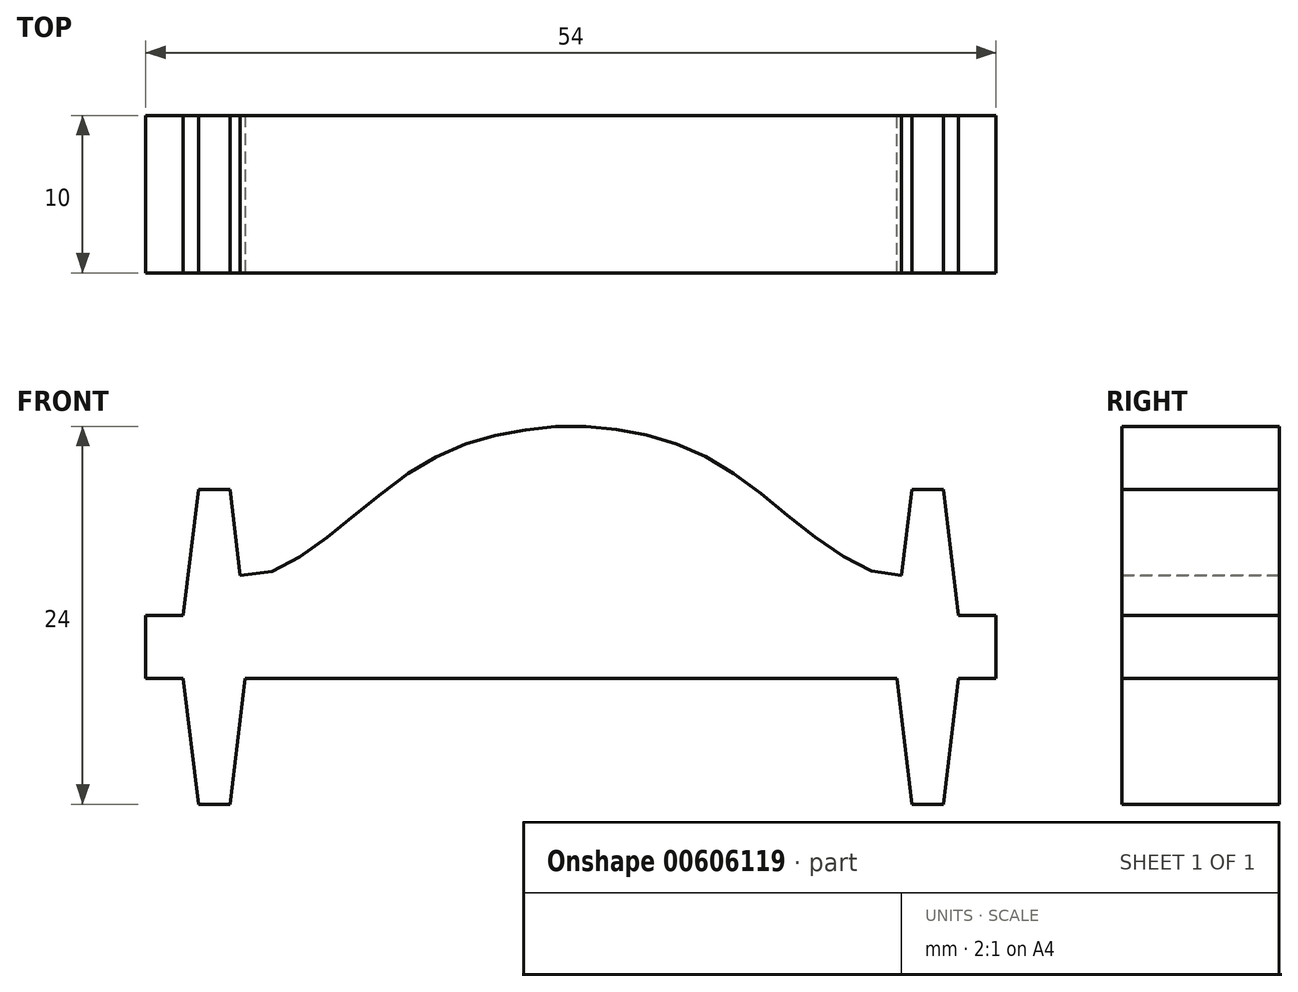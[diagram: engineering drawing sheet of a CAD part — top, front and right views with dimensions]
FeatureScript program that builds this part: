
annotation { "Feature Type Name" : "Feature", "Feature Type Description" : "" }
export const myFeature = defineFeature(function(context is Context, id is Id, definition is map)
    precondition{}
    {
        {
            var Q0;
            Q0=qCreatedBy(makeId("Front.planeOp"),FACE);
            var sketch = newSketch(context, id + "F0", { "sketchPlane" : qUnion([Q0])});
            skLineSegment(sketch, "E0", {"start": v(21, 26.44) * mm, "end": v(-21, 26.44) * mm});
            skFitSpline(sketch, "E1", {"points": [v(-21, 28.98) * mm, v(-17.48, 29.98) * mm, v(-13.98, 32.6) * mm, v(-10.48, 35.33) * mm, v(-6.98, 37.21) * mm, v(-3.48, 38.13) * mm, v(0, 38.44) * mm, v(3.5, 38.13) * mm, v(7, 37.21) * mm, v(10.5, 35.33) * mm, v(14, 32.6) * mm, v(17.63, 29.98) * mm, v(21, 28.98) * mm], "startDerivative": vector(52.28, -5.2) * mm, "endDerivative": vector(46.1, 5.3) * mm});
            skLineSegment(sketch, "E2", {"start": v(-21, 28.98) * mm, "end": v(-21, 26.44) * mm});
            skLineSegment(sketch, "E3", {"start": v(21, 28.98) * mm, "end": v(21, 26.44) * mm});
            skLineSegment(sketch, "E4", {"start": v(-3.48, 38.13) * mm, "end": v(3.5, 38.13) * mm, "construction": true});
            skLineSegment(sketch, "E5", {"start": v(7, 37.21) * mm, "end": v(-6.98, 37.21) * mm, "construction": true});
            skLineSegment(sketch, "E6", {"start": v(-10.48, 35.33) * mm, "end": v(10.5, 35.33) * mm, "construction": true});
            skLineSegment(sketch, "E7", {"start": v(14, 32.6) * mm, "end": v(-13.98, 32.6) * mm, "construction": true});
            skLineSegment(sketch, "E8", {"start": v(-17.48, 29.98) * mm, "end": v(17.63, 29.98) * mm, "construction": true});
            skSolve(sketch);
        }
        {
            var Q0;
            Q0=qCreatedBy(makeId("Front.planeOp"),FACE);
            var sketch = newSketch(context, id + "F1", { "sketchPlane" : qUnion([Q0])});
            skLineSegment(sketch, "E9", {"start": v(-27, 26.44) * mm, "end": v(27, 26.44) * mm});
            skLineSegment(sketch, "E10", {"start": v(27, 26.44) * mm, "end": v(27, 22.44) * mm});
            skLineSegment(sketch, "E11", {"start": v(27, 22.44) * mm, "end": v(-27, 22.44) * mm});
            skLineSegment(sketch, "E12", {"start": v(-27, 22.44) * mm, "end": v(-27, 26.44) * mm});
            skPoint(sketch, "E13", {"position": v(0, 22.44) * mm});
            skSolve(sketch);
        }
        {
            var Q0;
            Q0 = qSketchRegion(id + "F1", true);
            extrude(context, id + "F2", {"entities" : qUnion([Q0]), "endBound" : BoundingType.SYMMETRIC, "depth" : 10 * mm, "offsetDistance" : 25 * mm});
        }
        {
            var Q0;
            Q0=qCreatedBy(makeId("Front.planeOp"),FACE);
            var sketch = newSketch(context, id + "F3", { "sketchPlane" : qUnion([Q0])});
            skLineSegment(sketch, "E14", {"start": v(20.46, 24.44) * mm, "end": v(21.66, 34.44) * mm});
            skLineSegment(sketch, "E15", {"start": v(21.66, 34.44) * mm, "end": v(23.66, 34.44) * mm});
            skLineSegment(sketch, "E16", {"start": v(23.66, 14.44) * mm, "end": v(21.66, 14.44) * mm});
            skLineSegment(sketch, "E17", {"start": v(21.66, 14.44) * mm, "end": v(20.46, 24.44) * mm});
            skLineSegment(sketch, "E18", {"start": v(23.66, 34.44) * mm, "end": v(24.86, 24.44) * mm});
            skLineSegment(sketch, "E19", {"start": v(24.86, 24.44) * mm, "end": v(23.66, 14.44) * mm});
            skSolve(sketch);
        }
        {
            var Q0;
            Q0 = qSketchRegion(id + "F3", true);
            extrude(context, id + "F4", {"entities" : qUnion([Q0]), "endBound" : BoundingType.SYMMETRIC, "depth" : 10 * mm, "offsetDistance" : 25 * mm});
        }
        {
            var Q0;
            Q0=makeQuery(id+"F4.opExtrude","SWEPT_BODY",BODY,{"disambiguationData":[OSD([sQuery(id+"F3.wireOp",EDGE,"E14"),sQuery(id+"F3.wireOp",EDGE,"E15"),sQuery(id+"F3.wireOp",EDGE,"AWuQHskK-lmDN-hpRk-DwbA-gf0Xq94j8xVS"),sQuery(id+"F3.wireOp",EDGE,"E16"),sQuery(id+"F3.wireOp",EDGE,"E17")])]});
            var Q1;
            Q1=qCreatedBy(makeId("Right.planeOp"),FACE);
            mirror(context, id + "F5", {"operationType" : NewBodyOperationType.ADD, "entities" : qUnion([Q0]), "mirrorPlane" : qUnion([Q1])});
        }
        {
            var Q0;
            Q0=makeQuery(id+"F0.imprint","IMPRINT",FACE,{"disambiguationData":[TD([[makeQuery(id+"F0.imprint","IMPRINT",EDGE,{"derivedFrom":sQuery(id+"F0.wireOp",EDGE,"E0")}),-1.0]])]});
            var Q1;
            Q1=sQuery(id+"F0.wireOp",EDGE,"E1");
            extrude(context, id + "F6", {"entities" : qUnion([Q0]), "operationType" : NewBodyOperationType.ADD, "surfaceEntities" : qUnion([Q1]), "endBound" : BoundingType.SYMMETRIC, "depth" : 10 * mm, "offsetDistance" : 25 * mm});
        }
    });
